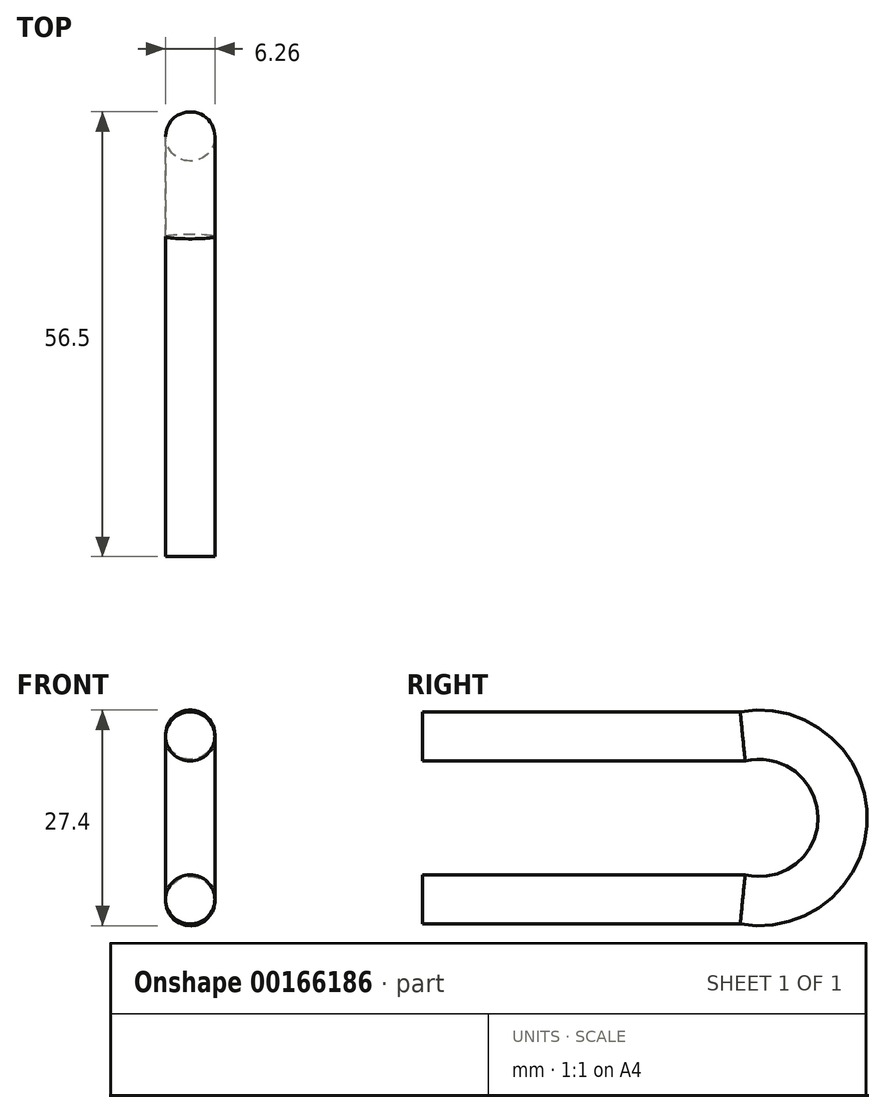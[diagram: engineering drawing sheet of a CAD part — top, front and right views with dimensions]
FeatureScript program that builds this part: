
annotation { "Feature Type Name" : "Feature", "Feature Type Description" : "" }
export const myFeature = defineFeature(function(context is Context, id is Id, definition is map)
    precondition{}
    {
        {
            var Q0;
            Q0=qCreatedBy(makeId("Right.planeOp"),FACE);
            var sketch = newSketch(context, id + "F0", { "sketchPlane" : qUnion([Q0])});
            skArc(sketch, "E0", {"start": v(40.66, -20.7) * mm, "mid": v(53.37, -10.35) * mm, "end": v(40.66, 0) * mm});
            skLineSegment(sketch, "E1", {"start": v(40.66, -20.7) * mm, "end": v(0, -20.7) * mm});
            skLineSegment(sketch, "E2", {"start": v(40.66, 0) * mm, "end": v(0, 0) * mm});
            skSolve(sketch);
        }
        {
            var Q0;
            Q0=qCreatedBy(makeId("Front.planeOp"),FACE);
            var sketch = newSketch(context, id + "F1", { "sketchPlane" : qUnion([Q0])});
            skCircle(sketch, "E3", {"center": v(0, 0) * mm, "radius": 3.13 * mm});
            skSolve(sketch);
        }
        {
            var Q0;
            Q0=makeQuery(id+"F1.imprint","IMPRINT",FACE,{"disambiguationData":[TD([[makeQuery(id+"F1.imprint","IMPRINT",EDGE,{"derivedFrom":sQuery(id+"F1.wireOp",EDGE,"E3")}),1.0]])]});
            var Q1;
            Q1=sQuery(id+"F0.wireOp",EDGE,"E2");
            var Q2;
            Q2=sQuery(id+"F0.wireOp",EDGE,"E0");
            var Q3;
            Q3=sQuery(id+"F0.wireOp",EDGE,"E1");
            sweep(context, id + "F2", {"profiles" : qUnion([Q0]), "path" : qUnion([Q1, Q2, Q3])});
        }
    });
